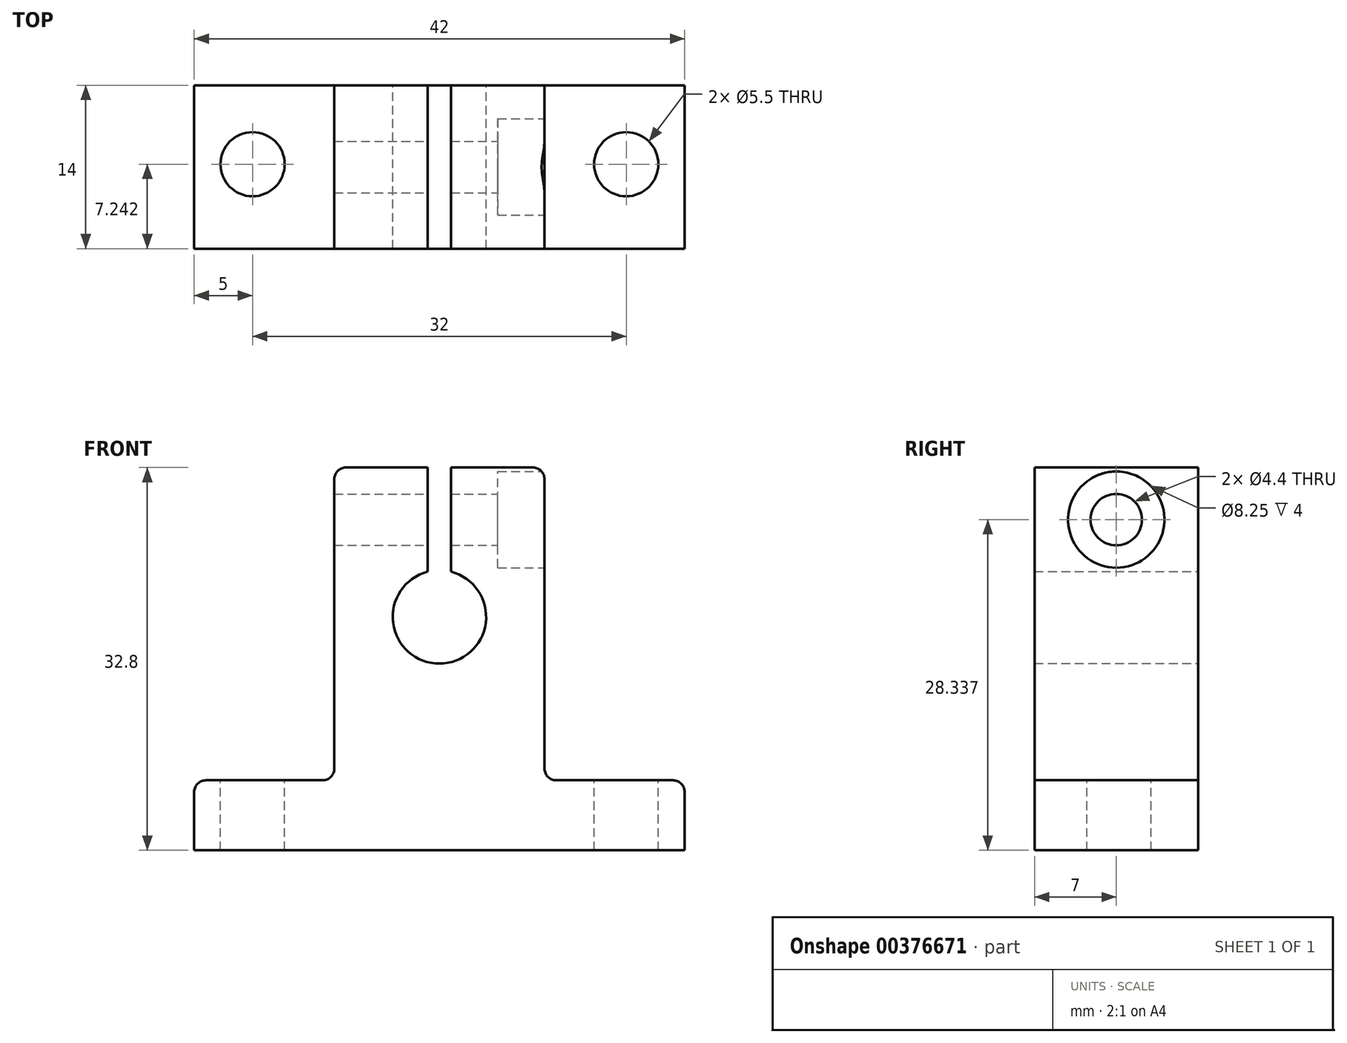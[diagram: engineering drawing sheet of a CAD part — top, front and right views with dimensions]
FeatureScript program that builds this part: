
annotation { "Feature Type Name" : "Feature", "Feature Type Description" : "" }
export const myFeature = defineFeature(function(context is Context, id is Id, definition is map)
    precondition{}
    {
        {
            var Q0;
            Q0=qCreatedBy(makeId("Front.planeOp"),FACE);
            var sketch = newSketch(context, id + "F0", { "sketchPlane" : qUnion([Q0])});
            skLineSegment(sketch, "E0.bottom", {"start": v(-21, 0) * mm, "end": v(21, 0) * mm});
            skLineSegment(sketch, "E0.top", {"start": v(-21, 6) * mm, "end": v(-9, 6) * mm});
            skLineSegment(sketch, "E0.left", {"start": v(-21, 0) * mm, "end": v(-21, 6) * mm});
            skLineSegment(sketch, "E0.right", {"start": v(21, 0) * mm, "end": v(21, 6) * mm});
            skPoint(sketch, "E1", {"position": v(0, 0) * mm});
            skLineSegment(sketch, "E2.top", {"start": v(-9, 32.8) * mm, "end": v(9, 32.8) * mm});
            skLineSegment(sketch, "E2.left", {"start": v(-9, 6) * mm, "end": v(-9, 32.8) * mm});
            skLineSegment(sketch, "E2.right", {"start": v(9, 6) * mm, "end": v(9, 32.8) * mm});
            skPoint(sketch, "E3", {"position": v(0, 6) * mm});
            skLineSegment(sketch, "E4", {"start": v(0, 0) * mm, "end": v(0, 40) * mm, "construction": true});
            skLineSegment(sketch, "E5.trimOffspring", {"start": v(9, 6) * mm, "end": v(21, 6) * mm});
            skCircle(sketch, "E6", {"center": v(0, 20) * mm, "radius": 4 * mm});
            skLineSegment(sketch, "E7.bottom", {"start": v(-1, 32.8) * mm, "end": v(1, 32.8) * mm});
            skLineSegment(sketch, "E7.top", {"start": v(-1, 23.87) * mm, "end": v(1, 23.87) * mm});
            skLineSegment(sketch, "E7.left", {"start": v(-1, 32.8) * mm, "end": v(-1, 23.87) * mm});
            skLineSegment(sketch, "E7.right", {"start": v(1, 32.8) * mm, "end": v(1, 23.87) * mm});
            skSolve(sketch);
        }
        {
            var Q0;
            Q0=makeQuery(id+"F0.imprint","IMPRINT",FACE,{"disambiguationData":[TD([[makeQuery(id+"F0.imprint","IMPRINT",EDGE,{"derivedFrom":sQuery(id+"F0.wireOp",EDGE,"E0.bottom")}),1.0]])]});
            extrude(context, id + "F1", {"entities" : qUnion([Q0]), "depth" : 14 * mm, "offsetDistance" : 25 * mm});
        }
        {
            var Q0;
            Q0=makeQuery(id+"F1.opExtrude","SWEPT_FACE",FACE,{"disambiguationData":[OSD([sQuery(id+"F0.wireOp",EDGE,"E2.right")])]});
            var sketch = newSketch(context, id + "F2", { "sketchPlane" : qUnion([Q0])});
            skPoint(sketch, "E8", {"position": v(-7, 28.34) * mm});
            skPoint(sketch, "E9", {"position": v(-7, 32.8) * mm});
            skLineSegment(sketch, "E10", {"start": v(-7, 28.34) * mm, "end": v(-7, 32.8) * mm, "construction": true});
            skPoint(sketch, "E11.0", {"position": v(-14, 28.34) * mm});
            skLineSegment(sketch, "E12", {"start": v(-7, 28.34) * mm, "end": v(-14, 28.34) * mm, "construction": true});
            skSolve(sketch);
        }
        {
            var Q0;
            Q0=sQuery(id+"F2.wireOp",VERTEX,"E8");
            var Q1;
            Q1=makeQuery(id+"F1.opExtrude","SWEPT_BODY",BODY,{"disambiguationData":[OSD([sQuery(id+"F0.wireOp",EDGE,"E0.bottom"),sQuery(id+"F0.wireOp",EDGE,"E0.top"),sQuery(id+"F0.wireOp",EDGE,"E0.left"),sQuery(id+"F0.wireOp",EDGE,"E0.right"),sQuery(id+"F0.wireOp",EDGE,"E2.top"),sQuery(id+"F0.wireOp",EDGE,"E2.left"),sQuery(id+"F0.wireOp",EDGE,"E2.right"),sQuery(id+"F0.wireOp",EDGE,"E5.trimOffspring"),sQuery(id+"F0.wireOp",EDGE,"E6"),sQuery(id+"F0.wireOp",EDGE,"E7.left"),sQuery(id+"F0.wireOp",EDGE,"E7.right")])]});
            hole(context, id + "F3", {"style" : HoleStyle.C_BORE, "endStyle" : HoleEndStyle.THROUGH, "standardTappedOrClearance" : lookupTablePath({ "standard" : "ISO", "fit" : "Normal", "size" : "M4", "type" : "Clearance" }), "standardBlindInLast" : lookupTablePath({ "fit" : "Standard", "standard" : "ISO", "size" : "M4", "type" : "Clearance" }), "holeDiameter" : 4.4 * mm, "cBoreDiameter" : 8.25 * mm, "cBoreDepth" : 4 * mm, "majorDiameter" : 5 * mm, "tappedDepth" : 12 * mm, "tapClearance" : 3, "startFromSketch" : true, "locations" : qUnion([Q0]), "scope" : qUnion([Q1])});
        }
        {
            var Q0;
            Q0=makeQuery(id+"F1.opExtrude","SWEPT_EDGE",EDGE,{"disambiguationData":[OSD([sQuery(id+"F0.wireOp",EDGE,"E2.right"),sQuery(id+"F0.wireOp",EDGE,"E5.trimOffspring")])]});
            var Q1;
            Q1=makeQuery(id+"F1.opExtrude","SWEPT_EDGE",EDGE,{"disambiguationData":[OSD([sQuery(id+"F0.wireOp",EDGE,"E0.top"),sQuery(id+"F0.wireOp",EDGE,"E2.left")])]});
            var Q2;
            Q2=makeQuery(id+"F1.opExtrude","SWEPT_EDGE",EDGE,{"disambiguationData":[OSD([sQuery(id+"F0.wireOp",EDGE,"E0.top"),sQuery(id+"F0.wireOp",EDGE,"E0.left")])]});
            var Q3;
            Q3=makeQuery(id+"F1.opExtrude","SWEPT_EDGE",EDGE,{"disambiguationData":[OSD([sQuery(id+"F0.wireOp",EDGE,"E0.right"),sQuery(id+"F0.wireOp",EDGE,"E5.trimOffspring")])]});
            var Q4;
            Q4=makeQuery(id+"F1.opExtrude","SWEPT_EDGE",EDGE,{"disambiguationData":[OSD([sQuery(id+"F0.wireOp",EDGE,"E2.top"),sQuery(id+"F0.wireOp",EDGE,"E2.left")])]});
            var Q5;
            Q5=makeQuery(id+"F1.opExtrude","SWEPT_EDGE",EDGE,{"disambiguationData":[OSD([sQuery(id+"F0.wireOp",EDGE,"E2.top"),sQuery(id+"F0.wireOp",EDGE,"E2.right")])]});
            fillet(context, id + "F4", {"entities" : qUnion([Q0, Q1, Q2, Q3, Q4, Q5]), "radius" : 1 * mm, "tangentPropagation" : true, "allowEdgeOverflow" : false});
        }
        {
            var Q0;
            Q0=makeQuery(id+"F1.opExtrude","SWEPT_FACE",FACE,{"disambiguationData":[OSD([sQuery(id+"F0.wireOp",EDGE,"E0.top")])]});
            var sketch = newSketch(context, id + "F5", { "sketchPlane" : qUnion([Q0])});
            skPoint(sketch, "E13", {"position": v(-16, -6.76) * mm});
            skPoint(sketch, "E14", {"position": v(16, -6.76) * mm});
            skLineSegment(sketch, "E15", {"start": v(-16, -6.76) * mm, "end": v(16, -6.76) * mm, "construction": true});
            skPoint(sketch, "E16", {"position": v(0, -6.76) * mm});
            skSolve(sketch);
        }
        {
            var Q0;
            Q0=sQuery(id+"F5.wireOp",VERTEX,"E13");
            var Q1;
            Q1=sQuery(id+"F5.wireOp",VERTEX,"E14");
            var Q2;
            Q2=makeQuery(id+"F1.opExtrude","SWEPT_BODY",BODY,{"disambiguationData":[OSD([sQuery(id+"F0.wireOp",EDGE,"E0.bottom"),sQuery(id+"F0.wireOp",EDGE,"E0.top"),sQuery(id+"F0.wireOp",EDGE,"E0.left"),sQuery(id+"F0.wireOp",EDGE,"E0.right"),sQuery(id+"F0.wireOp",EDGE,"E2.top"),sQuery(id+"F0.wireOp",EDGE,"E2.left"),sQuery(id+"F0.wireOp",EDGE,"E2.right"),sQuery(id+"F0.wireOp",EDGE,"E5.trimOffspring"),sQuery(id+"F0.wireOp",EDGE,"E6"),sQuery(id+"F0.wireOp",EDGE,"E7.left"),sQuery(id+"F0.wireOp",EDGE,"E7.right")])]});
            hole(context, id + "F6", {"style" : HoleStyle.SIMPLE, "endStyle" : HoleEndStyle.THROUGH, "standardTappedOrClearance" : lookupTablePath({ "standard" : "ISO", "fit" : "Normal", "size" : "M5", "type" : "Clearance" }), "standardBlindInLast" : lookupTablePath({ "fit" : "Standard", "standard" : "ISO", "size" : "M5", "type" : "Clearance" }), "holeDiameter" : 5.5 * mm, "majorDiameter" : 5 * mm, "tappedDepth" : 12 * mm, "tapClearance" : 3, "startFromSketch" : true, "locations" : qUnion([Q0, Q1]), "scope" : qUnion([Q2])});
        }
    });
